# Revit family: 602-1-002-DN65-200
name_source: partatom
category: Pipe Accessories
units: mm (PartAtom-declared; Revit-internal decimal feet)

## family parameters
Always vertical = Yes
Cut with Voids When Loaded = No
Part Type = Valve - Breaks Into
Round Connector Dimension = Use Diameter
Shared = No
Work Plane-Based = No

## types (12) — shared parameters
DN065-80_68-85 = 602-085-106-6100
DN080-100_84-106 = 602-106-119-6100
DN100-100_84-106 = 602-106-133-6100
DN100-100_99-119 = 602-119-133-6100
DN100-125_109-113 = 602-119-157-6100
DN100-125_99-119 = 602-133-157-6100
DN100-150_109-133 = 602-133-183-6100
DN125-150_132-157 = 602-157-183-6100
DN150-150_157-183 = 602-183-201-6100
DN150-200_ 176-201 = 602-201-215-6100
DN150-200_176-201 = 602-201-242-6100
DN175 = No
DN200-200_193-215 = 602-215-242-6100
DN225 = No
Description_ = AVK UNIVERSAL SUPA® STEP COUPLING
F = 5 mm  [stored 0.0164042 ft]
Search_Table = 602-1-002-DN65-200
URL_product_pages = https://www.avkvalves.com
W1 = 32 mm  [stored 0.104987 ft]

## per-type parameters (varying)
- DN065-80_68-85: B2=95 mm  [stored 0.31168 ft]; Body_height=190 mm; Body_height_ref=178 mm; Cut=53 mm  [stored 0.173885 ft]; Cut_2=106 mm  [stored 0.347769 ft]; Cut_3=85 mm  [stored 0.278871 ft]; Cut_4=43 mm; D=80 mm  [stored 0.262467 ft]; D(Adddon)=88 mm; D2=54 mm  [stored 0.177165 ft]; D2(Addon)=63 mm  [stored 0.206693 ft]; D3=220 mm; D3(Addon)=242 mm; D4(Addon)=53 mm  [stored 0.173885 ft]; DN=65 mm  [stored 0.213255 ft]; DN065=Yes; DN080=No; DN100=No; DN125=No; DN150=No; DN200=No; ID=33 mm; L=217 mm; L1=100 mm  [stored 0.328084 ft]; PCD=185 mm; PCD(Addon)=102 mm; PCD/2=93 mm  [stored 0.305118 ft]; W2=105 mm  [stored 0.344488 ft]; W2(Addon)=108 mm  [stored 0.354331 ft]
- DN080-100_84-106: B2=95 mm  [stored 0.31168 ft]; Body_height=190 mm; Body_height_ref=178 mm; Cut=60 mm  [stored 0.19685 ft]; Cut_2=119 mm  [stored 0.39042 ft]; Cut_3=106 mm  [stored 0.347769 ft]; Cut_4=53 mm  [stored 0.173885 ft]; D=77 mm  [stored 0.252625 ft]; D(Adddon)=85 mm  [stored 0.278871 ft]; D2=61 mm; D2(Addon)=70 mm  [stored 0.229659 ft]; D3=226 mm; D3(Addon)=249 mm; D4(Addon)=63 mm  [stored 0.206693 ft]; DN=80 mm  [stored 0.262467 ft]; DN065=No; DN080=Yes; DN100=No; DN125=No; DN150=No; DN200=No; ID=40 mm  [stored 0.131234 ft]; L=217 mm; L1=100 mm  [stored 0.328084 ft]; PCD=190 mm; PCD(Addon)=105 mm  [stored 0.344488 ft]; PCD/2=95 mm  [stored 0.31168 ft]; W2=108 mm  [stored 0.354331 ft]; W2(Addon)=111 mm
- DN100-100_84-106: B2=98 mm; Body_height=195 mm; Body_height_ref=183 mm; Cut=67 mm; Cut_2=133 mm; Cut_3=106 mm  [stored 0.347769 ft]; Cut_4=53 mm  [stored 0.173885 ft]; D=93 mm  [stored 0.305118 ft]; D(Adddon)=102 mm; D2=68 mm; D2(Addon)=77 mm  [stored 0.252625 ft]; D3=244 mm; D3(Addon)=268 mm; D4(Addon)=63 mm  [stored 0.206693 ft]; DN=100 mm  [stored 0.328084 ft]; DN065=No; DN080=No; DN100=Yes; DN125=No; DN150=No; DN200=No; ID=50 mm  [stored 0.164042 ft]; L=217 mm; L1=100 mm  [stored 0.328084 ft]; PCD=208 mm; PCD(Addon)=114 mm; PCD/2=104 mm; W2=117 mm  [stored 0.383858 ft]; W2(Addon)=120 mm
- DN100-100_99-119: B2=98 mm; Body_height=195 mm; Body_height_ref=183 mm; Cut=67 mm; Cut_2=133 mm; Cut_3=119 mm  [stored 0.39042 ft]; Cut_4=60 mm  [stored 0.19685 ft]; D=93 mm  [stored 0.305118 ft]; D(Adddon)=102 mm; D2=68 mm; D2(Addon)=77 mm  [stored 0.252625 ft]; D3=244 mm; D3(Addon)=268 mm; D4(Addon)=70 mm  [stored 0.229659 ft]; DN=100 mm  [stored 0.328084 ft]; DN065=No; DN080=No; DN100=Yes; DN125=No; DN150=No; DN200=No; ID=50 mm  [stored 0.164042 ft]; L=217 mm; L1=100 mm  [stored 0.328084 ft]; PCD=208 mm; PCD(Addon)=114 mm; PCD/2=104 mm; W2=117 mm  [stored 0.383858 ft]; W2(Addon)=120 mm
- DN125-150_132-157: B2=105 mm  [stored 0.344488 ft]; Body_height=210 mm; Body_height_ref=198 mm; Cut=92 mm  [stored 0.301837 ft]; Cut_2=183 mm; Cut_3=157 mm; Cut_4=79 mm; D=120 mm; D(Adddon)=132 mm; D2=93 mm  [stored 0.305118 ft]; D2(Addon)=102 mm; D3=300 mm; D3(Addon)=330 mm; D4(Addon)=89 mm  [stored 0.291995 ft]; DN=150 mm; DN065=No; DN080=No; DN100=No; DN125=No; DN150=Yes; DN200=No; ID=75 mm; L=237 mm; L1=115 mm  [stored 0.377297 ft]; PCD=265 mm; PCD(Addon)=146 mm; PCD/2=133 mm; W2=145 mm; W2(Addon)=149 mm
- DN150-150_157-183: B2=105 mm  [stored 0.344488 ft]; Body_height=210 mm; Body_height_ref=198 mm; Cut=101 mm; Cut_2=201 mm; Cut_3=183 mm; Cut_4=92 mm  [stored 0.301837 ft]; D=123 mm; D(Adddon)=135 mm; D2=102 mm; D2(Addon)=111 mm; D3=327 mm; D3(Addon)=360 mm; D4(Addon)=102 mm; DN=175 mm; DN065=No; DN080=No; DN100=No; DN125=No; DN150=Yes; DN200=No; ID=88 mm; L=237 mm; L1=115 mm  [stored 0.377297 ft]; PCD=265 mm; PCD(Addon)=146 mm; PCD/2=133 mm; W2=159 mm; W2(Addon)=162 mm
- DN150-200_176-201: B2=115 mm  [stored 0.377297 ft]; Body_height=230 mm; Body_height_ref=218 mm; Cut=121 mm; Cut_2=242 mm; Cut_3=201 mm; Cut_4=101 mm; D=145 mm; D(Adddon)=160 mm; D2=122 mm; D2(Addon)=131 mm; D3=357 mm; D3(Addon)=393 mm; D4(Addon)=111 mm; DN=200 mm; DN065=No; DN080=No; DN100=No; DN125=No; DN150=No; DN200=Yes; ID=100 mm  [stored 0.328084 ft]; L=257 mm; L1=140 mm; PCD=315 mm; PCD(Addon)=173 mm; PCD/2=158 mm; W2=174 mm; W2(Addon)=178 mm
- DN200-200_193-215: B2=115 mm  [stored 0.377297 ft]; Body_height=230 mm; Body_height_ref=218 mm; Cut=121 mm; Cut_2=242 mm; Cut_3=215 mm; Cut_4=108 mm  [stored 0.354331 ft]; D=145 mm; D(Adddon)=160 mm; D2=122 mm; D2(Addon)=131 mm; D3=357 mm; D3(Addon)=393 mm; D4(Addon)=118 mm; DN=200 mm; DN065=No; DN080=No; DN100=No; DN125=No; DN150=No; DN200=Yes; ID=100 mm  [stored 0.328084 ft]; L=257 mm; L1=140 mm; PCD=315 mm; PCD(Addon)=173 mm; PCD/2=158 mm; W2=174 mm; W2(Addon)=178 mm
- DN100-125_109-113: B2=98 mm; Body_height=195 mm; Body_height_ref=183 mm; Cut=79 mm; Cut_2=157 mm; Cut_3=119 mm  [stored 0.39042 ft]; Cut_4=60 mm  [stored 0.19685 ft]; D=93 mm  [stored 0.305118 ft]; D(Adddon)=102 mm; D2=80 mm  [stored 0.262467 ft]; D2(Addon)=89 mm  [stored 0.291995 ft]; D3=270 mm; D3(Addon)=297 mm; D4(Addon)=70 mm  [stored 0.229659 ft]; DN=100 mm  [stored 0.328084 ft]; DN065=No; DN080=No; DN100=No; DN125=Yes; DN150=No; DN200=No; ID=50 mm  [stored 0.164042 ft]; L=217 mm; L1=100 mm  [stored 0.328084 ft]; PCD=235 mm; PCD(Addon)=129 mm; PCD/2=118 mm; W2=130 mm; W2(Addon)=133 mm
- DN100-125_99-119: B2=98 mm; Body_height=195 mm; Body_height_ref=183 mm; Cut=79 mm; Cut_2=157 mm; Cut_3=133 mm; Cut_4=67 mm; D=106 mm  [stored 0.347769 ft]; D(Adddon)=117 mm  [stored 0.383858 ft]; D2=80 mm  [stored 0.262467 ft]; D2(Addon)=89 mm  [stored 0.291995 ft]; D3=270 mm; D3(Addon)=297 mm; D4(Addon)=77 mm  [stored 0.252625 ft]; DN=125 mm; DN065=No; DN080=No; DN100=No; DN125=Yes; DN150=No; DN200=No; ID=63 mm  [stored 0.206693 ft]; L=217 mm; L1=100 mm  [stored 0.328084 ft]; PCD=235 mm; PCD(Addon)=129 mm; PCD/2=118 mm; W2=130 mm; W2(Addon)=133 mm
- DN100-150_109-133: B2=105 mm  [stored 0.344488 ft]; Body_height=210 mm; Body_height_ref=198 mm; Cut=92 mm  [stored 0.301837 ft]; Cut_2=183 mm; Cut_3=133 mm; Cut_4=67 mm; D=120 mm; D(Adddon)=132 mm; D2=93 mm  [stored 0.305118 ft]; D2(Addon)=102 mm; D3=300 mm; D3(Addon)=330 mm; D4(Addon)=77 mm  [stored 0.252625 ft]; DN=150 mm; DN065=No; DN080=No; DN100=No; DN125=No; DN150=Yes; DN200=No; ID=75 mm; L=237 mm; L1=115 mm  [stored 0.377297 ft]; PCD=265 mm; PCD(Addon)=146 mm; PCD/2=133 mm; W2=145 mm; W2(Addon)=149 mm
- DN150-200_ 176-201: B2=105 mm  [stored 0.344488 ft]; Body_height=210 mm; Body_height_ref=198 mm; Cut=108 mm  [stored 0.354331 ft]; Cut_2=215 mm; Cut_3=201 mm; Cut_4=101 mm; D=123 mm; D(Adddon)=135 mm; D2=109 mm; D2(Addon)=118 mm; D3=327 mm; D3(Addon)=360 mm; D4(Addon)=111 mm; DN=175 mm; DN065=No; DN080=No; DN100=No; DN125=No; DN150=Yes; DN200=No; ID=88 mm; L=237 mm; L1=115 mm  [stored 0.377297 ft]; PCD=265 mm; PCD(Addon)=146 mm; PCD/2=133 mm; W2=159 mm; W2(Addon)=162 mm

note: [stored X ft] marks values corroborated as IEEE doubles in the binary element streams (Revit-internal decimal feet)

## geometry (parser evidence)
native form markers: Sweep x20
no freeform markers — native parametric forms only
